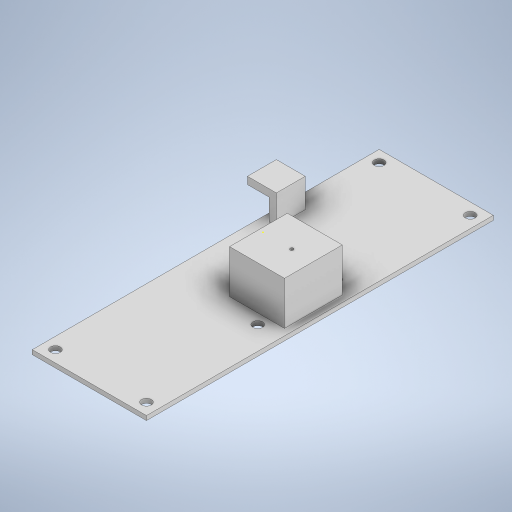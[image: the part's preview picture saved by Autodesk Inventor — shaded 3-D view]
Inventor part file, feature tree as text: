
AUTODESK INVENTOR PART (.ipt)
format: ipt  version: 2023 (Build 270158000, 158)  size: 343,552 bytes
history: native  units: mm
features: sketch x13, extrude x12
ambient origin geometry x8: Origin, YZ Plane, XZ Plane, XY Plane, X Axis, Y Axis, Z Axis, Center Point
bodies: Body1 (feature_tree)
feature tree (25):
  extrude  "Extrusion33"  Depth=240.0mm
  extrude  "Extrusion34"  Depth=38.0mm
  extrude  "Extrusion35"  Depth=30.0mm TaperAngle=0.0deg
  extrude  "Extrusion38"  Depth=30.0mm
  extrude  "Extrusion39"  Depth=15.0mm
  extrude  "Extrusion40"  Depth=3.5mm
  extrude  "Extrusion41"  Depth=35.0mm TaperAngle=0.0deg
  extrude  "Extrusion43"  Depth=20.0mm
  extrude  "Extrusion46"  Depth=20.0mm
  extrude  "Extrusion47"  Depth=5.0mm TaperAngle=0.0deg
  extrude  "Extrusion48"  Depth=10.0mm TaperAngle=0.0deg
  sketch  "Sketch71"  dims[d192=6.7mm d193=6.7mm]
  extrude  "Extrusion50"  Depth=6.7mm
  sketch  "Sketch44"  dims[d138=79.0mm d139=240.0mm]
  sketch  "Sketch45"  dims[d140=3.0mm d141=0.0mm d142=38.0mm]
  sketch  "Sketch47"  dims[d143=40.0mm d144=30.0mm d145=0.0mm]
  sketch  "Sketch58"  dims[d146=36.0mm d147=30.0mm d148=-2.617994mm]
  sketch  "Sketch59"  dims[d156=20.0mm d157=15.0mm]
  sketch  "Sketch60"  dims[d158=15.0mm d159=0.0mm d160=3.5mm]
  sketch  "Sketch61"  dims[d161=20.0mm d162=35.0mm d163=0.0mm]
  sketch  "Sketch65"  dims[d164=5.0mm d165=20.0mm]
  sketch  "Sketch68"  dims[d166=20.0mm d167=0.0mm d168=20.0mm]
  sketch  "Sketch69"  dims[d169=20.0mm d170=5.0mm d171=0.0mm]
  sketch  "Sketch70"  dims[d176=6.0mm d177=10.0mm d178=0.0mm]
  sketch  "Sketch73"  dims[d194=6.7mm d195=6.7mm d196=10.0mm d197=0.0mm d198=6.7mm d199=6.7mm d200=10.0mm d201=0.0mm d202=8.0mm d203=0.0mm d207=2.2mm d208=10.0mm d209=0.0mm d49=0.5mm d50=0.872665mm d51=0.5mm d52=0.872665mm d130=0.5mm d131=0.872665mm d132=0.5mm d133=0.872665mm d173=0.5mm d174=0.872665mm d175=0.5mm]
